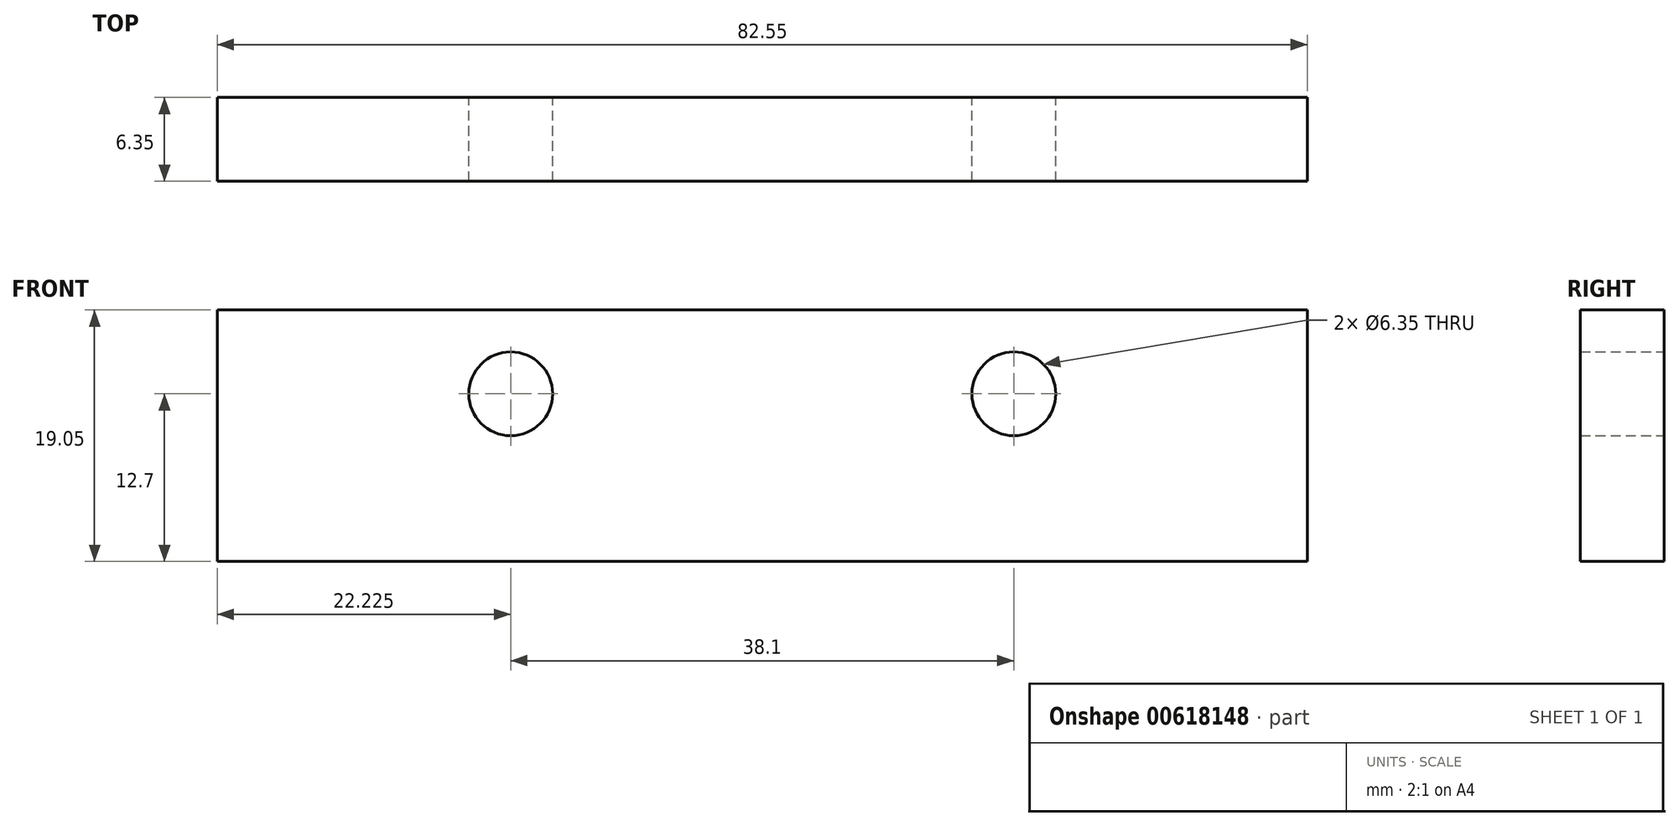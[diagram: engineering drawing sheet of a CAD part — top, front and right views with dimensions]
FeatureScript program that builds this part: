
annotation { "Feature Type Name" : "Feature", "Feature Type Description" : "" }
export const myFeature = defineFeature(function(context is Context, id is Id, definition is map)
    precondition{}
    {
        {
            var Q0;
            Q0=qCreatedBy(makeId("Front.planeOp"),FACE);
            var sketch = newSketch(context, id + "F0", { "sketchPlane" : qUnion([Q0])});
            skLineSegment(sketch, "E0.bottom", {"start": v(0, 0) * mm, "end": v(82.55, 0) * mm});
            skLineSegment(sketch, "E0.top", {"start": v(0, 19.05) * mm, "end": v(82.55, 19.05) * mm});
            skLineSegment(sketch, "E0.left", {"start": v(0, 0) * mm, "end": v(0, 19.05) * mm});
            skLineSegment(sketch, "E0.right", {"start": v(82.55, 0) * mm, "end": v(82.55, 19.05) * mm});
            skCircle(sketch, "E1", {"center": v(22.22, 12.7) * mm, "radius": 3.17 * mm});
            skCircle(sketch, "E2", {"center": v(60.33, 12.7) * mm, "radius": 3.18 * mm});
            skSolve(sketch);
        }
        {
            var Q0;
            Q0=qSketchRegion(id+"F0",true);
            extrude(context, id + "F1", {"entities" : qUnion([Q0]), "depth" : 6.35 * mm});
        }
    });
